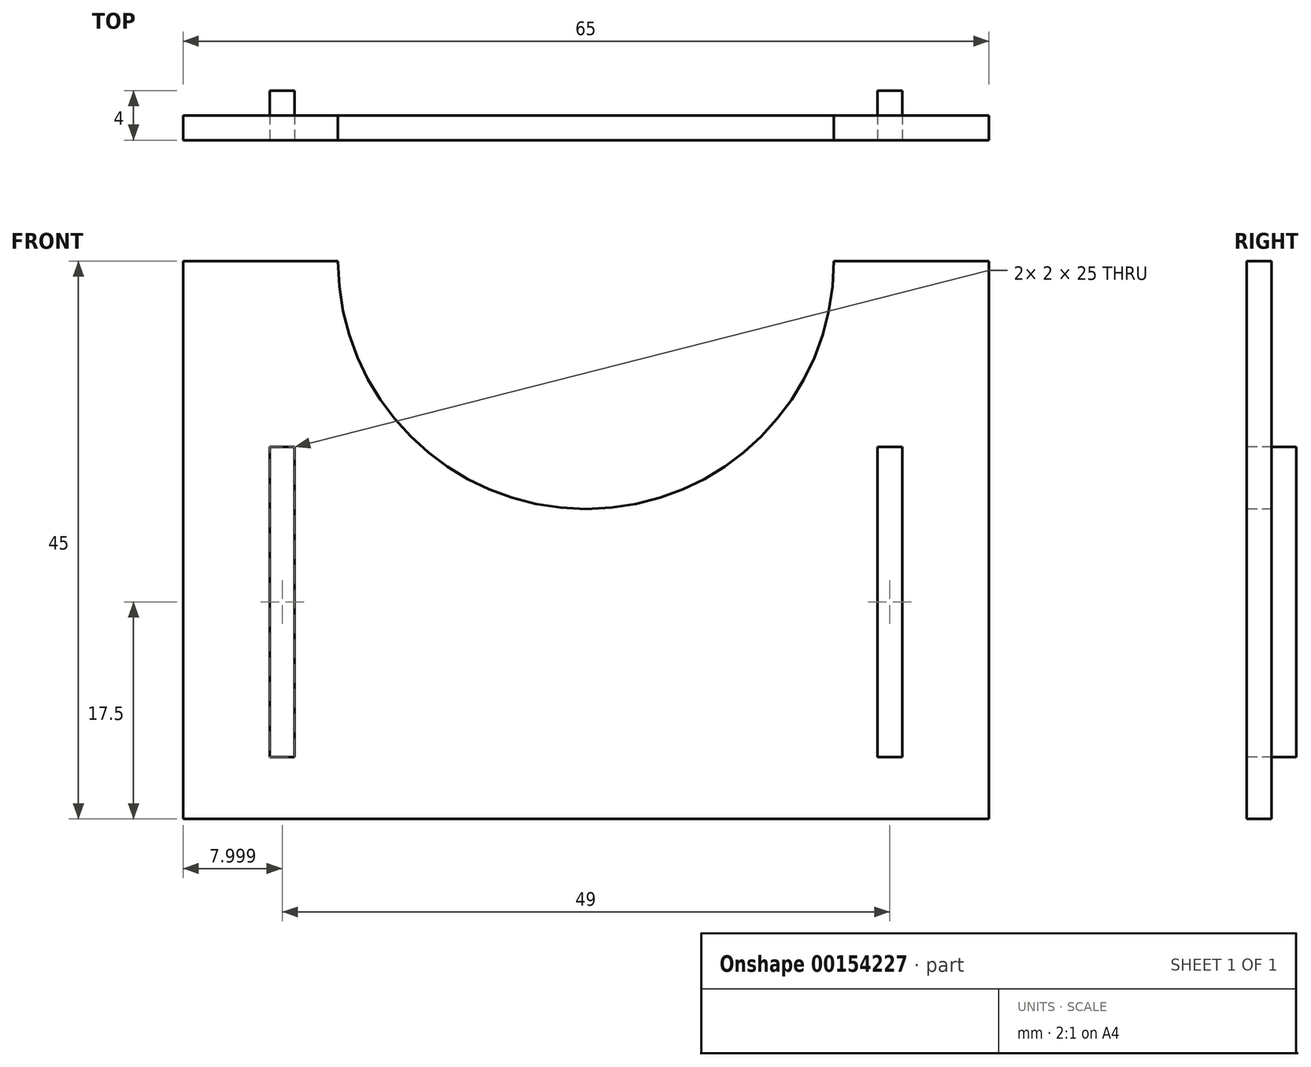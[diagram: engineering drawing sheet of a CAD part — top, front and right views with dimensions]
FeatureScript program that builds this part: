
annotation { "Feature Type Name" : "Feature", "Feature Type Description" : "" }
export const myFeature = defineFeature(function(context is Context, id is Id, definition is map)
    precondition{}
    {
        {
            var Q0;
            Q0=qCreatedBy(makeId("Front.planeOp"),FACE);
            var sketch = newSketch(context, id + "F0", { "sketchPlane" : qUnion([Q0])});
            skLineSegment(sketch, "E0.top", {"start": v(-34.52, 0) * mm, "end": v(30.48, 0) * mm});
            skLineSegment(sketch, "E0.left", {"start": v(-34.52, 45) * mm, "end": v(-34.52, 0) * mm});
            skLineSegment(sketch, "E0.right", {"start": v(30.48, 45) * mm, "end": v(30.48, 0) * mm});
            skLineSegment(sketch, "E1.bottom", {"start": v(-27.52, 30) * mm, "end": v(-25.52, 30) * mm});
            skLineSegment(sketch, "E1.top", {"start": v(-27.52, 5) * mm, "end": v(-25.52, 5) * mm});
            skLineSegment(sketch, "E1.left", {"start": v(-27.52, 30) * mm, "end": v(-27.52, 5) * mm});
            skLineSegment(sketch, "E1.right", {"start": v(-25.52, 30) * mm, "end": v(-25.52, 5) * mm});
            skArc(sketch, "E2", {"start": v(-22.02, 45) * mm, "mid": v(-2.02, 25) * mm, "end": v(17.98, 45) * mm});
            skLineSegment(sketch, "E3", {"start": v(-34.52, 45) * mm, "end": v(-22.02, 45) * mm});
            skLineSegment(sketch, "E4", {"start": v(17.98, 45) * mm, "end": v(30.48, 45) * mm});
            skLineSegment(sketch, "E5.bottom", {"start": v(21.48, 30) * mm, "end": v(23.48, 30) * mm});
            skLineSegment(sketch, "E5.top", {"start": v(21.48, 5) * mm, "end": v(23.48, 5) * mm});
            skLineSegment(sketch, "E5.left", {"start": v(21.48, 30) * mm, "end": v(21.48, 5) * mm});
            skLineSegment(sketch, "E5.right", {"start": v(23.48, 30) * mm, "end": v(23.48, 5) * mm});
            skSolve(sketch);
        }
        {
            var Q0;
            Q0=makeQuery(id+"F0.imprint","IMPRINT",FACE,{"disambiguationData":[TD([[makeQuery(id+"F0.imprint","IMPRINT",EDGE,{"derivedFrom":sQuery(id+"F0.wireOp",EDGE,"E1.bottom")}),-1.0]])]});
            var Q1;
            Q1=makeQuery(id+"F0.imprint","IMPRINT",FACE,{"disambiguationData":[TD([[makeQuery(id+"F0.imprint","IMPRINT",EDGE,{"derivedFrom":sQuery(id+"F0.wireOp",EDGE,"E5.bottom")}),-1.0]])]});
            extrude(context, id + "F1", {"entities" : qUnion([Q0, Q1]), "oppositeDirection" : true, "depth" : 4 * mm});
        }
        {
            var Q0;
            Q0 = qSketchRegion(id + "F0", true);
            extrude(context, id + "F2", {"entities" : qUnion([Q0]), "oppositeDirection" : true, "depth" : 2 * mm});
        }
    });
